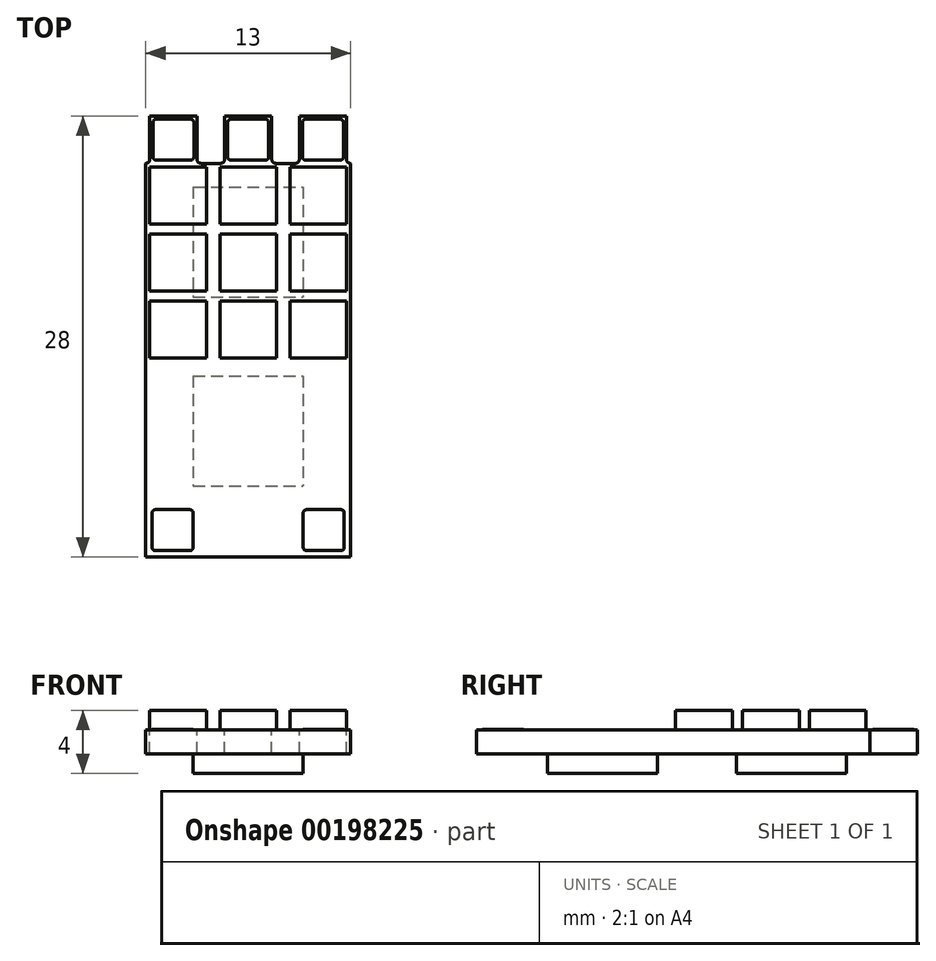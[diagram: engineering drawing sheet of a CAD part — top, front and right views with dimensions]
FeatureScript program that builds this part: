
annotation { "Feature Type Name" : "Feature", "Feature Type Description" : "" }
export const myFeature = defineFeature(function(context is Context, id is Id, definition is map)
    precondition{}
    {
        {
            var Q0;
            Q0=qCreatedBy(makeId("Top.planeOp"),FACE);
            var sketch = newSketch(context, id + "F0", { "sketchPlane" : qUnion([Q0])});
            skLineSegment(sketch, "E0.bottom", {"start": v(-6.5, 14) * mm, "end": v(6.5, 14) * mm});
            skLineSegment(sketch, "E0.top", {"start": v(-6.5, -14) * mm, "end": v(6.5, -14) * mm});
            skLineSegment(sketch, "E0.left", {"start": v(-6.5, 14) * mm, "end": v(-6.5, -14) * mm});
            skLineSegment(sketch, "E0.right", {"start": v(6.5, 14) * mm, "end": v(6.5, -14) * mm});
            skSolve(sketch);
        }
        {
            var Q0;
            Q0=makeQuery(id+"F0.imprint","IMPRINT",FACE,{"disambiguationData":[TD([[makeQuery(id+"F0.imprint","IMPRINT",EDGE,{"derivedFrom":sQuery(id+"F0.wireOp",EDGE,"E0.bottom")}),-1.0]])]});
            extrude(context, id + "F1", {"entities" : qUnion([Q0]), "depth" : 1.5 * mm});
        }
        {
            var Q0;
            Q0=makeQuery(id+"F1.opExtrude","CAP_FACE",FACE,{"disambiguationData":[OSD([sQuery(id+"F0.wireOp",EDGE,"E0.bottom"),sQuery(id+"F0.wireOp",EDGE,"E0.top"),sQuery(id+"F0.wireOp",EDGE,"E0.left"),sQuery(id+"F0.wireOp",EDGE,"E0.right")])],"isStart":false});
            var sketch = newSketch(context, id + "F2", { "sketchPlane" : qUnion([Q0])});
            skLineSegment(sketch, "E1.bottom", {"start": v(-3.25, 14) * mm, "end": v(-1.5, 14) * mm});
            skLineSegment(sketch, "E1.top", {"start": v(-3.25, 11) * mm, "end": v(-1.5, 11) * mm});
            skLineSegment(sketch, "E1.left", {"start": v(-3.25, 14) * mm, "end": v(-3.25, 11) * mm});
            skLineSegment(sketch, "E1.right", {"start": v(-1.5, 14) * mm, "end": v(-1.5, 11) * mm});
            skLineSegment(sketch, "E2.bottom", {"start": v(1.5, 14) * mm, "end": v(3.25, 14) * mm});
            skLineSegment(sketch, "E2.top", {"start": v(1.5, 11) * mm, "end": v(3.25, 11) * mm});
            skLineSegment(sketch, "E2.left", {"start": v(1.5, 14) * mm, "end": v(1.5, 11) * mm});
            skLineSegment(sketch, "E2.right", {"start": v(3.25, 14) * mm, "end": v(3.25, 11) * mm});
            skLineSegment(sketch, "E3.bottom", {"start": v(-6.5, 14) * mm, "end": v(-6.25, 14) * mm});
            skLineSegment(sketch, "E3.top", {"start": v(-6.5, 11) * mm, "end": v(-6.25, 11) * mm});
            skLineSegment(sketch, "E3.left", {"start": v(-6.5, 14) * mm, "end": v(-6.5, 11) * mm});
            skLineSegment(sketch, "E3.right", {"start": v(-6.25, 14) * mm, "end": v(-6.25, 11) * mm});
            skPoint(sketch, "E4.oppositeSnap0", {"position": v(-2.38, 11) * mm});
            skLineSegment(sketch, "E4.bottom", {"start": v(6.5, 14) * mm, "end": v(6.25, 14) * mm});
            skLineSegment(sketch, "E4.top", {"start": v(6.5, 11) * mm, "end": v(6.25, 11) * mm});
            skLineSegment(sketch, "E4.left", {"start": v(6.5, 14) * mm, "end": v(6.5, 11) * mm});
            skLineSegment(sketch, "E4.right", {"start": v(6.25, 14) * mm, "end": v(6.25, 11) * mm});
            skSolve(sketch);
        }
        {
            var Q0;
            Q0 = qSketchRegion(id + "F2", true);
            extrude(context, id + "F3", {"entities" : qUnion([Q0]), "operationType" : NewBodyOperationType.REMOVE, "oppositeDirection" : true, "depth" : 25 * mm});
        }
        {
            var Q0;
            Q0=makeQuery(id+"F1.opExtrude","CAP_FACE",FACE,{"disambiguationData":[OSD([sQuery(id+"F0.wireOp",EDGE,"E0.bottom"),sQuery(id+"F0.wireOp",EDGE,"E0.top"),sQuery(id+"F0.wireOp",EDGE,"E0.left"),sQuery(id+"F0.wireOp",EDGE,"E0.right")])],"isStart":false});
            var sketch = newSketch(context, id + "F4", { "sketchPlane" : qUnion([Q0])});
            skLineSegment(sketch, "E5.bottom", {"start": v(-6.05, 13.8) * mm, "end": v(-3.45, 13.8) * mm});
            skLineSegment(sketch, "E5.top", {"start": v(-6.05, 11.2) * mm, "end": v(-3.45, 11.2) * mm});
            skLineSegment(sketch, "E5.left", {"start": v(-6.05, 13.8) * mm, "end": v(-6.05, 11.2) * mm});
            skLineSegment(sketch, "E5.right", {"start": v(-3.45, 13.8) * mm, "end": v(-3.45, 11.2) * mm});
            skLineSegment(sketch, "E6.bottom", {"start": v(-1.3, 13.8) * mm, "end": v(1.3, 13.8) * mm});
            skLineSegment(sketch, "E6.top", {"start": v(-1.3, 11.2) * mm, "end": v(1.3, 11.2) * mm});
            skLineSegment(sketch, "E6.left", {"start": v(-1.3, 13.8) * mm, "end": v(-1.3, 11.2) * mm});
            skLineSegment(sketch, "E6.right", {"start": v(1.3, 13.8) * mm, "end": v(1.3, 11.2) * mm});
            skLineSegment(sketch, "E7.bottom", {"start": v(3.45, 13.8) * mm, "end": v(6.05, 13.8) * mm});
            skLineSegment(sketch, "E7.top", {"start": v(3.45, 11.2) * mm, "end": v(6.05, 11.2) * mm});
            skLineSegment(sketch, "E7.left", {"start": v(3.45, 13.8) * mm, "end": v(3.45, 11.2) * mm});
            skLineSegment(sketch, "E7.right", {"start": v(6.05, 13.8) * mm, "end": v(6.05, 11.2) * mm});
            skSolve(sketch);
        }
        {
            var Q0;
            Q0=makeQuery(id+"F4.imprint","IMPRINT",FACE,{"disambiguationData":[TD([[makeQuery(id+"F4.imprint","IMPRINT",EDGE,{"derivedFrom":sQuery(id+"F4.wireOp",EDGE,"E5.bottom")}),-1.0]])]});
            var Q1;
            Q1=makeQuery(id+"F4.imprint","IMPRINT",FACE,{"disambiguationData":[TD([[makeQuery(id+"F4.imprint","IMPRINT",EDGE,{"derivedFrom":sQuery(id+"F4.wireOp",EDGE,"E6.bottom")}),-1.0]])]});
            var Q2;
            Q2=makeQuery(id+"F4.imprint","IMPRINT",FACE,{"disambiguationData":[TD([[makeQuery(id+"F4.imprint","IMPRINT",EDGE,{"derivedFrom":sQuery(id+"F4.wireOp",EDGE,"E7.bottom")}),-1.0]])]});
            extrude(context, id + "F5", {"entities" : qUnion([Q0, Q1, Q2]), "operationType" : NewBodyOperationType.ADD, "depth" : 0.05 * mm});
        }
        {
            var Q0;
            Q0=makeQuery(id+"F5.opExtrude","SWEPT_EDGE",EDGE,{"disambiguationData":[OSD([sQuery(id+"F4.wireOp",EDGE,"E5.top"),sQuery(id+"F4.wireOp",EDGE,"E5.left")])]});
            var Q1;
            Q1=makeQuery(id+"F5.opExtrude","SWEPT_EDGE",EDGE,{"disambiguationData":[OSD([sQuery(id+"F4.wireOp",EDGE,"E5.bottom"),sQuery(id+"F4.wireOp",EDGE,"E5.left")])]});
            var Q2;
            Q2=makeQuery(id+"F5.opExtrude","SWEPT_EDGE",EDGE,{"disambiguationData":[OSD([sQuery(id+"F4.wireOp",EDGE,"E5.top"),sQuery(id+"F4.wireOp",EDGE,"E5.right")])]});
            var Q3;
            Q3=makeQuery(id+"F5.opExtrude","SWEPT_EDGE",EDGE,{"disambiguationData":[OSD([sQuery(id+"F4.wireOp",EDGE,"E5.bottom"),sQuery(id+"F4.wireOp",EDGE,"E5.right")])]});
            var Q4;
            Q4=makeQuery(id+"F5.opExtrude","SWEPT_EDGE",EDGE,{"disambiguationData":[OSD([sQuery(id+"F4.wireOp",EDGE,"E6.bottom"),sQuery(id+"F4.wireOp",EDGE,"E6.right")])]});
            var Q5;
            Q5=makeQuery(id+"F5.opExtrude","SWEPT_EDGE",EDGE,{"disambiguationData":[OSD([sQuery(id+"F4.wireOp",EDGE,"E6.bottom"),sQuery(id+"F4.wireOp",EDGE,"E6.left")])]});
            var Q6;
            Q6=makeQuery(id+"F5.opExtrude","SWEPT_EDGE",EDGE,{"disambiguationData":[OSD([sQuery(id+"F4.wireOp",EDGE,"E6.top"),sQuery(id+"F4.wireOp",EDGE,"E6.right")])]});
            var Q7;
            Q7=makeQuery(id+"F5.opExtrude","SWEPT_EDGE",EDGE,{"disambiguationData":[OSD([sQuery(id+"F4.wireOp",EDGE,"E7.bottom"),sQuery(id+"F4.wireOp",EDGE,"E7.left")])]});
            var Q8;
            Q8=makeQuery(id+"F5.opExtrude","SWEPT_EDGE",EDGE,{"disambiguationData":[OSD([sQuery(id+"F4.wireOp",EDGE,"E7.bottom"),sQuery(id+"F4.wireOp",EDGE,"E7.right")])]});
            var Q9;
            Q9=makeQuery(id+"F5.opExtrude","SWEPT_EDGE",EDGE,{"disambiguationData":[OSD([sQuery(id+"F4.wireOp",EDGE,"E7.top"),sQuery(id+"F4.wireOp",EDGE,"E7.right")])]});
            var Q10;
            Q10=makeQuery(id+"F5.opExtrude","SWEPT_EDGE",EDGE,{"disambiguationData":[OSD([sQuery(id+"F4.wireOp",EDGE,"E6.top"),sQuery(id+"F4.wireOp",EDGE,"E6.left")])]});
            var Q11;
            Q11=makeQuery(id+"F5.opExtrude","SWEPT_EDGE",EDGE,{"disambiguationData":[OSD([sQuery(id+"F4.wireOp",EDGE,"E7.top"),sQuery(id+"F4.wireOp",EDGE,"E7.left")])]});
            fillet(context, id + "F6", {"entities" : qUnion([Q0, Q1, Q2, Q3, Q4, Q5, Q6, Q7, Q8, Q9, Q10, Q11]), "radius" : 0.2 * mm, "tangentPropagation" : true, "allowEdgeOverflow" : false});
        }
        {
            var Q0;
            Q0=makeQuery(id+"F3.boolean.opBoolean","COPY",EDGE,{"derivedFrom":makeQuery(id+"F3.opExtrude","SWEPT_EDGE",EDGE,{"disambiguationData":[OSD([sQuery(id+"F2.wireOp",EDGE,"E4.top"),sQuery(id+"F2.wireOp",EDGE,"E4.right")])]})});
            var Q1;
            Q1=makeQuery(id+"F3.boolean.opBoolean","COPY",EDGE,{"derivedFrom":makeQuery(id+"F3.opExtrude","SWEPT_EDGE",EDGE,{"disambiguationData":[OSD([sQuery(id+"F2.wireOp",EDGE,"E3.top"),sQuery(id+"F2.wireOp",EDGE,"E3.right")])]})});
            var Q2;
            Q2=makeQuery(id+"F3.boolean.opBoolean","COPY",EDGE,{"derivedFrom":makeQuery(id+"F3.opExtrude","SWEPT_EDGE",EDGE,{"disambiguationData":[OSD([sQuery(id+"F2.wireOp",EDGE,"E1.top"),sQuery(id+"F2.wireOp",EDGE,"E1.right")])]})});
            var Q3;
            Q3=makeQuery(id+"F3.boolean.opBoolean","COPY",EDGE,{"derivedFrom":makeQuery(id+"F3.opExtrude","SWEPT_EDGE",EDGE,{"disambiguationData":[OSD([sQuery(id+"F2.wireOp",EDGE,"E2.top"),sQuery(id+"F2.wireOp",EDGE,"E2.right")])]})});
            var Q4;
            Q4=makeQuery(id+"F3.boolean.opBoolean","COPY",EDGE,{"derivedFrom":makeQuery(id+"F3.opExtrude","SWEPT_EDGE",EDGE,{"disambiguationData":[OSD([sQuery(id+"F2.wireOp",EDGE,"E1.top"),sQuery(id+"F2.wireOp",EDGE,"E1.left")])]})});
            var Q5;
            Q5=makeQuery(id+"F3.boolean.opBoolean","COPY",EDGE,{"derivedFrom":makeQuery(id+"F3.opExtrude","SWEPT_EDGE",EDGE,{"disambiguationData":[OSD([sQuery(id+"F2.wireOp",EDGE,"E2.top"),sQuery(id+"F2.wireOp",EDGE,"E2.left")])]})});
            fillet(context, id + "F7", {"entities" : qUnion([Q0, Q1, Q2, Q3, Q4, Q5]), "radius" : 0.25 * mm, "tangentPropagation" : true, "allowEdgeOverflow" : false});
        }
        {
            var Q0;
            Q0=makeQuery(id+"F1.opExtrude","CAP_FACE",FACE,{"disambiguationData":[OSD([sQuery(id+"F0.wireOp",EDGE,"E0.bottom"),sQuery(id+"F0.wireOp",EDGE,"E0.top"),sQuery(id+"F0.wireOp",EDGE,"E0.left"),sQuery(id+"F0.wireOp",EDGE,"E0.right")])],"isStart":false});
            var sketch = newSketch(context, id + "F8", { "sketchPlane" : qUnion([Q0])});
            skLineSegment(sketch, "E8.bottom", {"start": v(-6.1, -11) * mm, "end": v(-3.5, -11) * mm});
            skLineSegment(sketch, "E8.top", {"start": v(-6.1, -13.6) * mm, "end": v(-3.5, -13.6) * mm});
            skLineSegment(sketch, "E8.left", {"start": v(-6.1, -11) * mm, "end": v(-6.1, -13.6) * mm});
            skLineSegment(sketch, "E8.right", {"start": v(-3.5, -11) * mm, "end": v(-3.5, -13.6) * mm});
            skLineSegment(sketch, "E9.bottom", {"start": v(3.5, -11) * mm, "end": v(6.1, -11) * mm});
            skLineSegment(sketch, "E9.top", {"start": v(3.5, -13.6) * mm, "end": v(6.1, -13.6) * mm});
            skLineSegment(sketch, "E9.left", {"start": v(3.5, -11) * mm, "end": v(3.5, -13.6) * mm});
            skLineSegment(sketch, "E9.right", {"start": v(6.1, -11) * mm, "end": v(6.1, -13.6) * mm});
            skSolve(sketch);
        }
        {
            var Q0;
            Q0=makeQuery(id+"F8.imprint","IMPRINT",FACE,{"disambiguationData":[TD([[makeQuery(id+"F8.imprint","IMPRINT",EDGE,{"derivedFrom":sQuery(id+"F8.wireOp",EDGE,"E8.bottom")}),-1.0]])]});
            var Q1;
            Q1=makeQuery(id+"F8.imprint","IMPRINT",FACE,{"disambiguationData":[TD([[makeQuery(id+"F8.imprint","IMPRINT",EDGE,{"derivedFrom":sQuery(id+"F8.wireOp",EDGE,"E9.bottom")}),-1.0]])]});
            extrude(context, id + "F9", {"entities" : qUnion([Q0, Q1]), "operationType" : NewBodyOperationType.ADD, "depth" : 0.05 * mm});
        }
        {
            var Q0;
            Q0=makeQuery(id+"F9.opExtrude","SWEPT_EDGE",EDGE,{"disambiguationData":[OSD([sQuery(id+"F8.wireOp",EDGE,"E8.top"),sQuery(id+"F8.wireOp",EDGE,"E8.left")])]});
            var Q1;
            Q1=makeQuery(id+"F9.opExtrude","SWEPT_EDGE",EDGE,{"disambiguationData":[OSD([sQuery(id+"F8.wireOp",EDGE,"E8.top"),sQuery(id+"F8.wireOp",EDGE,"E8.right")])]});
            var Q2;
            Q2=makeQuery(id+"F9.opExtrude","SWEPT_EDGE",EDGE,{"disambiguationData":[OSD([sQuery(id+"F8.wireOp",EDGE,"E8.bottom"),sQuery(id+"F8.wireOp",EDGE,"E8.left")])]});
            var Q3;
            Q3=makeQuery(id+"F9.opExtrude","SWEPT_EDGE",EDGE,{"disambiguationData":[OSD([sQuery(id+"F8.wireOp",EDGE,"E9.top"),sQuery(id+"F8.wireOp",EDGE,"E9.left")])]});
            var Q4;
            Q4=makeQuery(id+"F9.opExtrude","SWEPT_EDGE",EDGE,{"disambiguationData":[OSD([sQuery(id+"F8.wireOp",EDGE,"E9.top"),sQuery(id+"F8.wireOp",EDGE,"E9.right")])]});
            var Q5;
            Q5=makeQuery(id+"F9.opExtrude","SWEPT_EDGE",EDGE,{"disambiguationData":[OSD([sQuery(id+"F8.wireOp",EDGE,"E9.bottom"),sQuery(id+"F8.wireOp",EDGE,"E9.left")])]});
            var Q6;
            Q6=makeQuery(id+"F9.opExtrude","SWEPT_EDGE",EDGE,{"disambiguationData":[OSD([sQuery(id+"F8.wireOp",EDGE,"E8.bottom"),sQuery(id+"F8.wireOp",EDGE,"E8.right")])]});
            var Q7;
            Q7=makeQuery(id+"F9.opExtrude","SWEPT_EDGE",EDGE,{"disambiguationData":[OSD([sQuery(id+"F8.wireOp",EDGE,"E9.bottom"),sQuery(id+"F8.wireOp",EDGE,"E9.right")])]});
            fillet(context, id + "F10", {"entities" : qUnion([Q0, Q1, Q2, Q3, Q4, Q5, Q6, Q7]), "radius" : 0.2 * mm, "tangentPropagation" : true, "allowEdgeOverflow" : false});
        }
        {
            var Q0;
            Q0=makeQuery(id+"F1.opExtrude","CAP_FACE",FACE,{"disambiguationData":[OSD([sQuery(id+"F0.wireOp",EDGE,"E0.bottom"),sQuery(id+"F0.wireOp",EDGE,"E0.top"),sQuery(id+"F0.wireOp",EDGE,"E0.left"),sQuery(id+"F0.wireOp",EDGE,"E0.right")])],"isStart":false});
            var sketch = newSketch(context, id + "F11", { "sketchPlane" : qUnion([Q0])});
            skLineSegment(sketch, "E10.bottom", {"start": v(-6.25, 10.75) * mm, "end": v(-2.65, 10.75) * mm});
            skLineSegment(sketch, "E10.top", {"start": v(-6.25, 7.15) * mm, "end": v(-2.65, 7.15) * mm});
            skLineSegment(sketch, "E10.left", {"start": v(-6.25, 10.75) * mm, "end": v(-6.25, 7.15) * mm});
            skLineSegment(sketch, "E10.right", {"start": v(-2.65, 10.75) * mm, "end": v(-2.65, 7.15) * mm});
            skLineSegment(sketch, "E11.bottom", {"start": v(-1.8, 10.75) * mm, "end": v(1.8, 10.75) * mm});
            skLineSegment(sketch, "E11.top", {"start": v(-1.8, 7.15) * mm, "end": v(1.8, 7.15) * mm});
            skLineSegment(sketch, "E11.left", {"start": v(-1.8, 10.75) * mm, "end": v(-1.8, 7.15) * mm});
            skLineSegment(sketch, "E11.right", {"start": v(1.8, 10.75) * mm, "end": v(1.8, 7.15) * mm});
            skLineSegment(sketch, "E12.bottom", {"start": v(2.65, 10.75) * mm, "end": v(6.25, 10.75) * mm});
            skLineSegment(sketch, "E12.top", {"start": v(2.65, 7.15) * mm, "end": v(6.25, 7.15) * mm});
            skLineSegment(sketch, "E12.left", {"start": v(2.65, 10.75) * mm, "end": v(2.65, 7.15) * mm});
            skLineSegment(sketch, "E12.right", {"start": v(6.25, 10.75) * mm, "end": v(6.25, 7.15) * mm});
            skLineSegment(sketch, "E13.0.1.0", {"start": v(2.65, 2.9) * mm, "end": v(6.25, 2.9) * mm});
            skLineSegment(sketch, "E13.0.1.1", {"start": v(2.65, 6.5) * mm, "end": v(2.65, 2.9) * mm});
            skLineSegment(sketch, "E13.0.1.2", {"start": v(2.65, 6.5) * mm, "end": v(6.25, 6.5) * mm});
            skLineSegment(sketch, "E13.0.1.3", {"start": v(1.8, 6.5) * mm, "end": v(1.8, 2.9) * mm});
            skLineSegment(sketch, "E13.0.1.4", {"start": v(-1.8, 6.5) * mm, "end": v(-1.8, 2.9) * mm});
            skLineSegment(sketch, "E13.0.1.5", {"start": v(-1.8, 2.9) * mm, "end": v(1.8, 2.9) * mm});
            skLineSegment(sketch, "E13.0.1.6", {"start": v(6.25, 6.5) * mm, "end": v(6.25, 2.9) * mm});
            skLineSegment(sketch, "E13.0.1.7", {"start": v(-1.8, 6.5) * mm, "end": v(1.8, 6.5) * mm});
            skLineSegment(sketch, "E13.0.1.8", {"start": v(-2.65, 6.5) * mm, "end": v(-2.65, 2.9) * mm});
            skLineSegment(sketch, "E13.0.1.9", {"start": v(-6.25, 6.5) * mm, "end": v(-6.25, 2.9) * mm});
            skLineSegment(sketch, "E13.0.1.10", {"start": v(-6.25, 2.9) * mm, "end": v(-2.65, 2.9) * mm});
            skLineSegment(sketch, "E13.0.1.11", {"start": v(-6.25, 6.5) * mm, "end": v(-2.65, 6.5) * mm});
            skLineSegment(sketch, "E13.0.2.0", {"start": v(2.65, -1.35) * mm, "end": v(6.25, -1.35) * mm});
            skLineSegment(sketch, "E13.0.2.1", {"start": v(2.65, 2.25) * mm, "end": v(2.65, -1.35) * mm});
            skLineSegment(sketch, "E13.0.2.2", {"start": v(2.65, 2.25) * mm, "end": v(6.25, 2.25) * mm});
            skLineSegment(sketch, "E13.0.2.3", {"start": v(1.8, 2.25) * mm, "end": v(1.8, -1.35) * mm});
            skLineSegment(sketch, "E13.0.2.4", {"start": v(-1.8, 2.25) * mm, "end": v(-1.8, -1.35) * mm});
            skLineSegment(sketch, "E13.0.2.5", {"start": v(-1.8, -1.35) * mm, "end": v(1.8, -1.35) * mm});
            skLineSegment(sketch, "E13.0.2.6", {"start": v(6.25, 2.25) * mm, "end": v(6.25, -1.35) * mm});
            skLineSegment(sketch, "E13.0.2.7", {"start": v(-1.8, 2.25) * mm, "end": v(1.8, 2.25) * mm});
            skLineSegment(sketch, "E13.0.2.8", {"start": v(-2.65, 2.25) * mm, "end": v(-2.65, -1.35) * mm});
            skLineSegment(sketch, "E13.0.2.9", {"start": v(-6.25, 2.25) * mm, "end": v(-6.25, -1.35) * mm});
            skLineSegment(sketch, "E13.0.2.10", {"start": v(-6.25, -1.35) * mm, "end": v(-2.65, -1.35) * mm});
            skLineSegment(sketch, "E13.0.2.11", {"start": v(-6.25, 2.25) * mm, "end": v(-2.65, 2.25) * mm});
            skLineSegment(sketch, "E13.direction1", {"start": v(-6.25, 7.15) * mm, "end": v(18.75, 7.15) * mm, "construction": true});
            skLineSegment(sketch, "E13.direction2", {"start": v(-6.25, 7.15) * mm, "end": v(-6.25, 2.9) * mm, "construction": true});
            skSolve(sketch);
        }
        {
            var Q0;
            Q0 = qSketchRegion(id + "F11", true);
            extrude(context, id + "F12", {"entities" : qUnion([Q0]), "operationType" : NewBodyOperationType.ADD, "depth" : 1.25 * mm});
        }
        {
            var Q0;
            Q0=makeQuery(id+"F1.opExtrude","CAP_FACE",FACE,{"disambiguationData":[OSD([sQuery(id+"F0.wireOp",EDGE,"E0.bottom"),sQuery(id+"F0.wireOp",EDGE,"E0.top"),sQuery(id+"F0.wireOp",EDGE,"E0.left"),sQuery(id+"F0.wireOp",EDGE,"E0.right")])],"isStart":true});
            var sketch = newSketch(context, id + "F13", { "sketchPlane" : qUnion([Q0])});
            skLineSegment(sketch, "E14.bottom", {"start": v(-3.5, -9.5) * mm, "end": v(3.5, -9.5) * mm});
            skLineSegment(sketch, "E14.top", {"start": v(-3.5, -2.5) * mm, "end": v(3.5, -2.5) * mm});
            skLineSegment(sketch, "E14.left", {"start": v(-3.5, -9.5) * mm, "end": v(-3.5, -2.5) * mm});
            skLineSegment(sketch, "E14.right", {"start": v(3.5, -9.5) * mm, "end": v(3.5, -2.5) * mm});
            skLineSegment(sketch, "E15.bottom", {"start": v(-3.5, 2.5) * mm, "end": v(3.5, 2.5) * mm});
            skLineSegment(sketch, "E15.top", {"start": v(-3.5, 9.5) * mm, "end": v(3.5, 9.5) * mm});
            skLineSegment(sketch, "E15.left", {"start": v(-3.5, 2.5) * mm, "end": v(-3.5, 9.5) * mm});
            skLineSegment(sketch, "E15.right", {"start": v(3.5, 2.5) * mm, "end": v(3.5, 9.5) * mm});
            skSolve(sketch);
        }
        {
            var Q0;
            Q0 = qSketchRegion(id + "F13", true);
            extrude(context, id + "F14", {"entities" : qUnion([Q0]), "operationType" : NewBodyOperationType.ADD, "depth" : 1.25 * mm});
        }
    });
